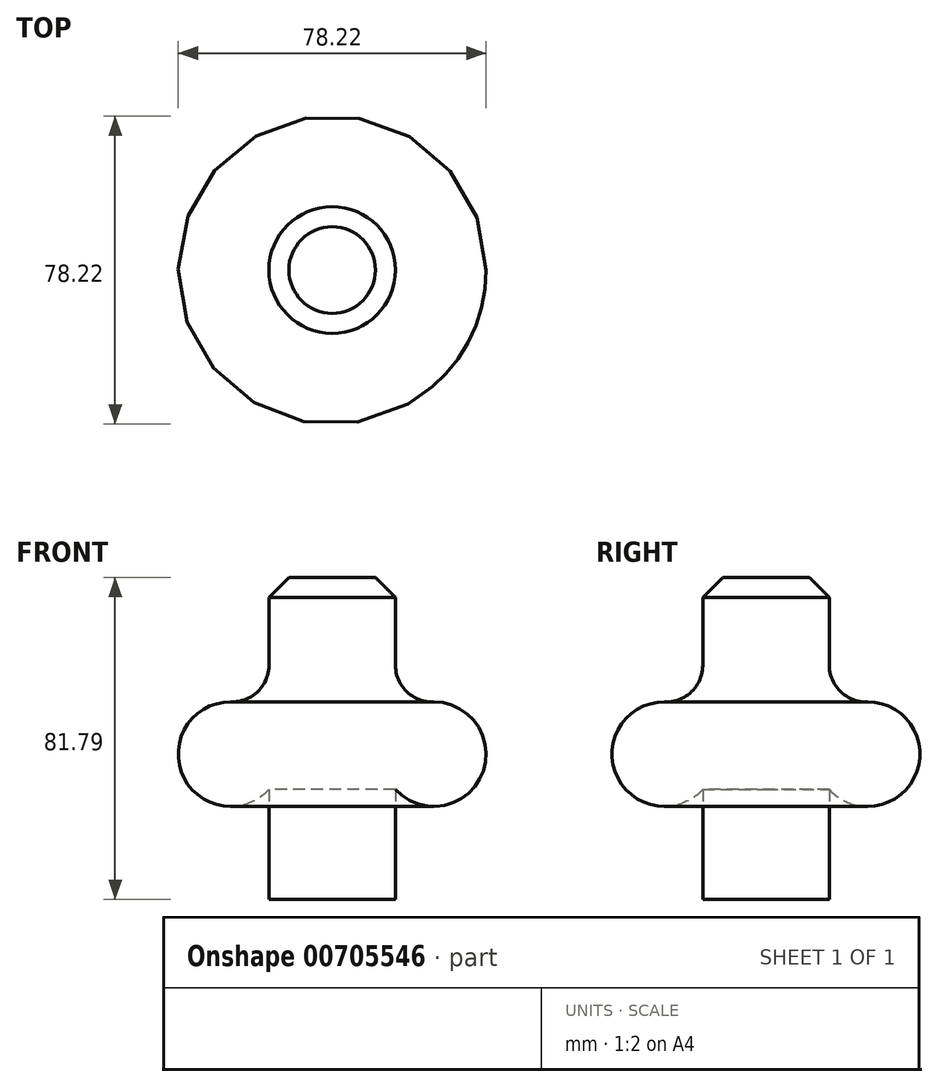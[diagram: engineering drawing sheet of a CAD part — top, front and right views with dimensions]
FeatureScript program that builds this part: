
annotation { "Feature Type Name" : "Feature", "Feature Type Description" : "" }
export const myFeature = defineFeature(function(context is Context, id is Id, definition is map)
    precondition{}
    {
        {
            var Q0;
            Q0=qCreatedBy(makeId("Front.planeOp"),FACE);
            var sketch = newSketch(context, id + "F0", { "sketchPlane" : qUnion([Q0])});
            skLineSegment(sketch, "E0", {"start": v(0, 59.1) * mm, "end": v(0, 0) * mm});
            skSolve(sketch);
        }
        {
            var Q0;
            Q0=qCreatedBy(makeId("Right.planeOp"),FACE);
            var sketch = newSketch(context, id + "F1", { "sketchPlane" : qUnion([Q0])});
            skCircle(sketch, "E1", {"center": v(-25.84, 36.91) * mm, "radius": 13.28 * mm});
            skSolve(sketch);
        }
        {
            var Q0;
            Q0=makeQuery(id+"F1.imprint","IMPRINT",FACE,{"disambiguationData":[TD([[makeQuery(id+"F1.imprint","IMPRINT",EDGE,{"derivedFrom":sQuery(id+"F1.wireOp",EDGE,"E1")}),1.0]])]});
            var Q1;
            Q1=sQuery(id+"F0.wireOp",EDGE,"E0");
            revolve(context, id + "F2", {"surfaceOperationType" : NewSurfaceOperationType.NEW, "entities" : qUnion([Q0]), "axis" : qUnion([Q1]), "revolveType" : RevolveType.FULL});
        }
        {
            var Q0;
            Q0=qCreatedBy(makeId("Top.planeOp"),FACE);
            var sketch = newSketch(context, id + "F3", { "sketchPlane" : qUnion([Q0])});
            skCircle(sketch, "E2", {"center": v(0, 0) * mm, "radius": 16.07 * mm});
            skSolve(sketch);
        }
        {
            var Q0;
            Q0=makeQuery(id+"F3.imprint","IMPRINT",FACE,{"disambiguationData":[TD([[makeQuery(id+"F3.imprint","IMPRINT",EDGE,{"derivedFrom":sQuery(id+"F3.wireOp",EDGE,"E2")}),1.0]])]});
            extrude(context, id + "F4", {"entities" : qUnion([Q0]), "operationType" : NewBodyOperationType.ADD, "depth" : 81.8 * mm, "offsetDistance" : 25.4 * mm});
        }
        {
            var Q0;
            Q0=makeQuery(id+"F4.boolean.opBoolean","INTERSECT",EDGE,{"disambiguationData":[OD(1.0)],"derivedFrom":[makeQuery(id+"F2.opRevolve","SWEPT_FACE",FACE,{"disambiguationData":[OSD([sQuery(id+"F1.wireOp",EDGE,"E1")])]}),makeQuery(id+"F4.opExtrude","SWEPT_FACE",FACE,{"disambiguationData":[OSD([sQuery(id+"F3.wireOp",EDGE,"E2")])]})]});
            fillet(context, id + "F5", {"entities" : qUnion([Q0]), "radius" : 9.3 * mm, "tangentPropagation" : true, "allowEdgeOverflow" : false});
        }
        {
            var Q0;
            Q0=makeQuery(id+"F4.opExtrude","CAP_EDGE",EDGE,{"disambiguationData":[OSD([sQuery(id+"F3.wireOp",EDGE,"E2")])],"isStart":false});
            chamfer(context, id + "F6", {"entities" : qUnion([Q0]), "width" : 5.08 * mm, "tangentPropagation" : true});
        }
    });
